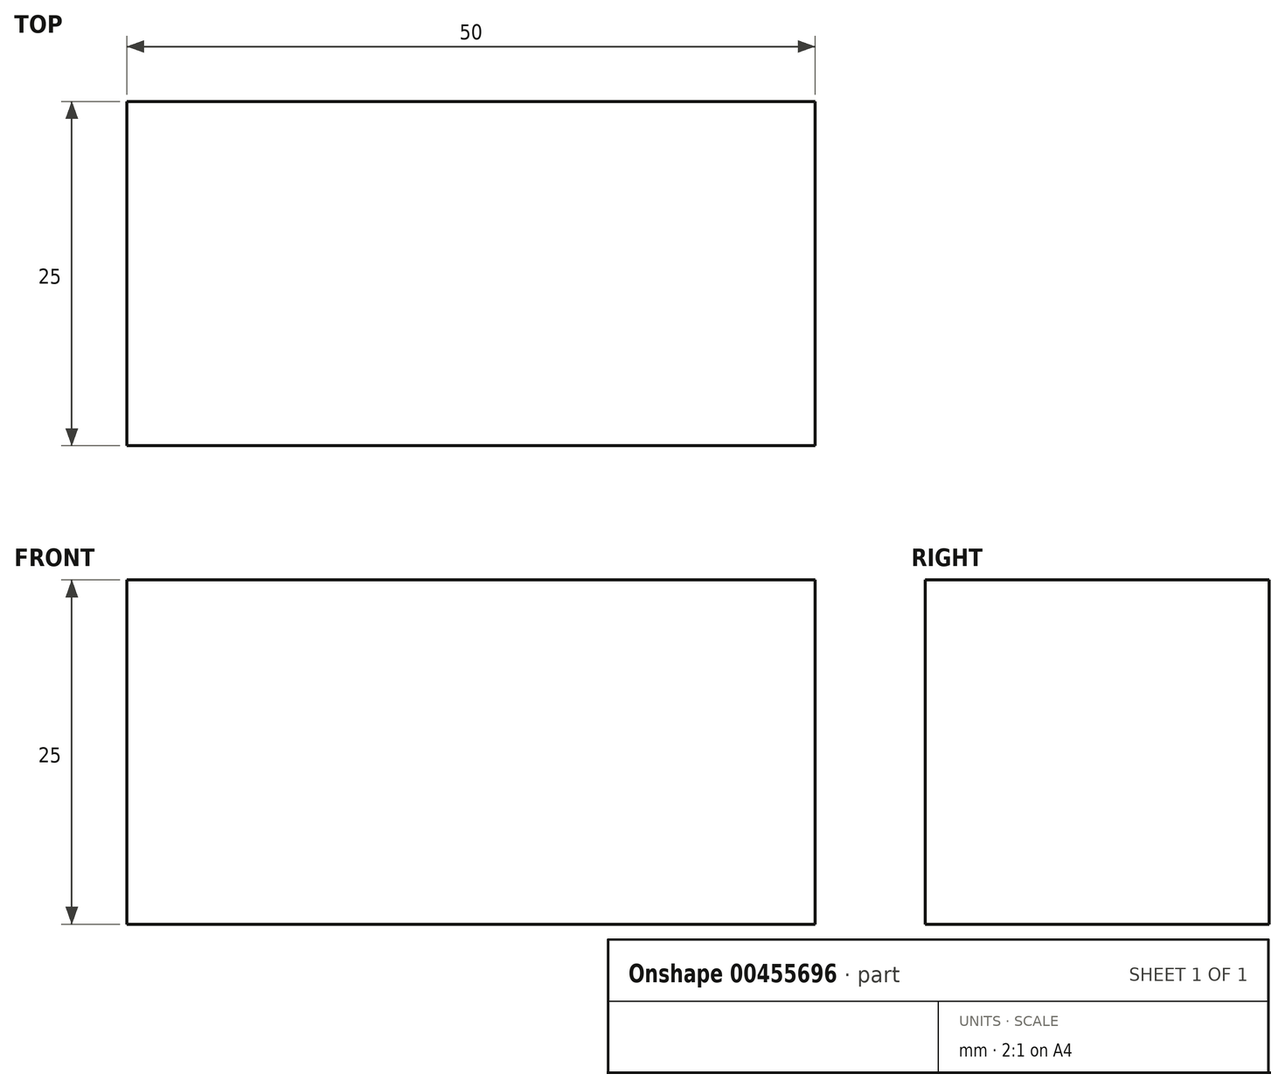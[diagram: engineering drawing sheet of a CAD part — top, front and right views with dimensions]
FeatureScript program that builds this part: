
annotation { "Feature Type Name" : "Feature", "Feature Type Description" : "" }
export const myFeature = defineFeature(function(context is Context, id is Id, definition is map)
    precondition{}
    {
        {
            var Q0;
            Q0=qCreatedBy(makeId("Top.planeOp"),FACE);
            var sketch = newSketch(context, id + "F0", { "sketchPlane" : qUnion([Q0])});
            skLineSegment(sketch, "E0.bottom", {"start": v(-25, 12.5) * mm, "end": v(25, 12.5) * mm});
            skLineSegment(sketch, "E0.top", {"start": v(-25, -12.5) * mm, "end": v(25, -12.5) * mm});
            skLineSegment(sketch, "E0.left", {"start": v(-25, 12.5) * mm, "end": v(-25, -12.5) * mm});
            skLineSegment(sketch, "E0.right", {"start": v(25, 12.5) * mm, "end": v(25, -12.5) * mm});
            skPoint(sketch, "E0.middle", {"position": v(0, 0) * mm});
            skSolve(sketch);
        }
        {
            var Q0;
            Q0=makeQuery(id+"F0.imprint","IMPRINT",FACE,{"disambiguationData":[TD([[makeQuery(id+"F0.imprint","IMPRINT",EDGE,{"derivedFrom":sQuery(id+"F0.wireOp",EDGE,"E0.bottom")}),-1.0]])]});
            extrude(context, id + "F1", {"entities" : qUnion([Q0]), "depth" : 25 * mm});
        }
    });
